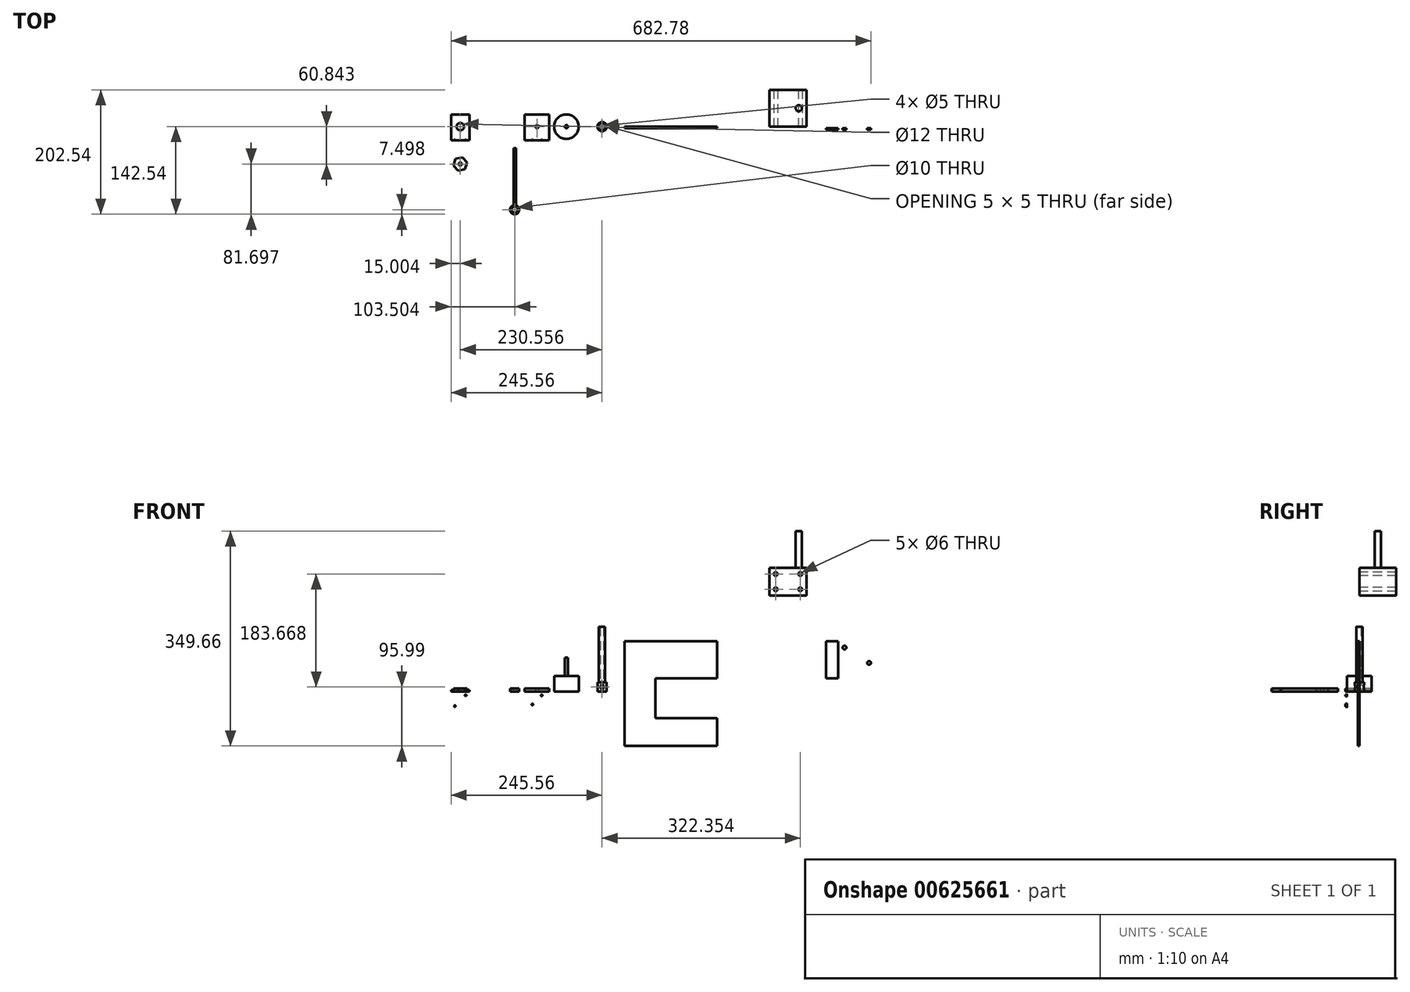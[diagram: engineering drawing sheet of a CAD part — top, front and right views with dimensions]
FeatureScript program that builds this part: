
annotation { "Feature Type Name" : "Feature", "Feature Type Description" : "" }
export const myFeature = defineFeature(function(context is Context, id is Id, definition is map)
    precondition{}
    {
        {
            var Q0;
            Q0=qCreatedBy(makeId("Top.planeOp"),FACE);
            var sketch = newSketch(context, id + "F0", { "sketchPlane" : qUnion([Q0])});
            skCircle(sketch, "E0", {"center": v(0, 0) * mm, "radius": 2.5 * mm});
            skCircle(sketch, "E1", {"center": v(0, 0) * mm, "radius": 7.5 * mm});
            skLineSegment(sketch, "E2", {"start": v(-20, 7.5) * mm, "end": v(20, 7.5) * mm});
            skCircle(sketch, "E3", {"center": v(-57.97, 0) * mm, "radius": 20 * mm});
            skLineSegment(sketch, "E4.bottom", {"start": v(-125.74, 20) * mm, "end": v(-85.74, 20) * mm});
            skLineSegment(sketch, "E4.top", {"start": v(-125.74, -20) * mm, "end": v(-85.74, -20) * mm});
            skLineSegment(sketch, "E4.left", {"start": v(-125.74, 20) * mm, "end": v(-125.74, -20) * mm});
            skLineSegment(sketch, "E4.right", {"start": v(-85.74, 20) * mm, "end": v(-85.74, -20) * mm});
            skPoint(sketch, "E4.middle", {"position": v(-105.74, 0) * mm});
            skCircle(sketch, "E5", {"center": v(-105.74, 0) * mm, "radius": 2.5 * mm});
            skLineSegment(sketch, "E6.bottom", {"start": v(-215.56, 20) * mm, "end": v(-245.56, 20) * mm});
            skLineSegment(sketch, "E6.top", {"start": v(-215.56, -20) * mm, "end": v(-245.56, -20) * mm});
            skLineSegment(sketch, "E6.left", {"start": v(-215.56, 20) * mm, "end": v(-215.56, -20) * mm});
            skLineSegment(sketch, "E6.right", {"start": v(-245.56, 20) * mm, "end": v(-245.56, -20) * mm});
            skCircle(sketch, "E7", {"center": v(-230.56, 0) * mm, "radius": 6 * mm});
            skPoint(sketch, "E7.centerSnap0", {"position": v(-230.56, 20) * mm});
            skCircle(sketch, "E8.cCircle", {"center": v(-230.56, -60.84) * mm, "radius": 9.88 * mm, "construction": true});
            skLineSegment(sketch, "E8.0", {"start": v(-219.4, -58.45) * mm, "end": v(-222.9, -69.3) * mm});
            skLineSegment(sketch, "E8.1", {"start": v(-222.9, -69.3) * mm, "end": v(-234.06, -71.7) * mm});
            skLineSegment(sketch, "E8.2", {"start": v(-234.06, -71.7) * mm, "end": v(-241.71, -63.24) * mm});
            skLineSegment(sketch, "E8.3", {"start": v(-241.71, -63.24) * mm, "end": v(-238.21, -52.38) * mm});
            skLineSegment(sketch, "E8.4", {"start": v(-238.21, -52.38) * mm, "end": v(-227.05, -49.98) * mm});
            skLineSegment(sketch, "E8.5", {"start": v(-227.05, -49.98) * mm, "end": v(-219.4, -58.45) * mm});
            skPoint(sketch, "E8.0.midPoint", {"position": v(-221.15, -63.88) * mm});
            skCircle(sketch, "E9", {"center": v(-230.56, -60.84) * mm, "radius": 2.5 * mm});
            skCircle(sketch, "E10", {"center": v(-142.06, -135.04) * mm, "radius": 5 * mm});
            skArc(sketch, "E11", {"start": v(-144.06, -127.81) * mm, "mid": v(-142.06, -142.54) * mm, "end": v(-140.06, -127.81) * mm});
            skLineSegment(sketch, "E12", {"start": v(-140.06, -127.81) * mm, "end": v(-140.06, -35.04) * mm});
            skLineSegment(sketch, "E13", {"start": v(-140.06, -35.04) * mm, "end": v(-142.06, -35.04) * mm});
            skLineSegment(sketch, "E14.MirrorCS", {"start": v(-144.06, -127.81) * mm, "end": v(-144.06, -35.04) * mm});
            skLineSegment(sketch, "E15", {"start": v(-142.06, -35.04) * mm, "end": v(-144.06, -35.04) * mm});
            skSolve(sketch);
        }
        {
            var Q0;
            Q0=makeQuery(id+"F0.imprint","IMPRINT",FACE,{"disambiguationData":[TD([[makeQuery(id+"F0.imprint","IMPRINT",EDGE,{"derivedFrom":sQuery(id+"F0.wireOp",EDGE,"E0")}),-1.0]])]});
            extrude(context, id + "F1", {"entities" : qUnion([Q0]), "depth" : 15 * mm, "offsetDistance" : 25 * mm});
        }
        {
            var Q0;
            Q0=makeQuery(id+"F1.opExtrude","CAP_FACE",FACE,{"disambiguationData":[OSD([sQuery(id+"F0.wireOp",EDGE,"E0"),sQuery(id+"F0.wireOp",EDGE,"E1")])],"isStart":false});
            var sketch = newSketch(context, id + "F2", { "sketchPlane" : qUnion([Q0])});
            skCircle(sketch, "E16", {"center": v(0, 0) * mm, "radius": 5 * mm});
            skSolve(sketch);
        }
        {
            var Q0;
            Q0=makeQuery(id+"F2.imprint","IMPRINT",FACE,{"disambiguationData":[TD([[makeQuery(id+"F2.imprint","IMPRINT",EDGE,{"derivedFrom":sQuery(id+"F2.wireOp",EDGE,"E16")}),1.0]])]});
            extrude(context, id + "F3", {"entities" : qUnion([Q0]), "operationType" : NewBodyOperationType.ADD, "depth" : 90 * mm, "offsetDistance" : 25 * mm});
        }
        {
            var Q0;
            Q0=sQuery(id+"F0.wireOp",EDGE,"E2");
            extrude(context, id + "F4", {"bodyType" : ToolBodyType.SURFACE, "surfaceEntities" : qUnion([Q0]), "depth" : 15 * mm, "offsetDistance" : 25 * mm});
        }
        {
            var Q0;
            Q0=makeQuery(id+"F4.opExtrude","SWEPT_FACE",FACE,{"disambiguationData":[OSD([sQuery(id+"F0.wireOp",EDGE,"E2")])]});
            var sketch = newSketch(context, id + "F5", { "sketchPlane" : qUnion([Q0])});
            skCircle(sketch, "E17", {"center": v(0, 7.5) * mm, "radius": 3 * mm});
            skPoint(sketch, "E17.centerSnap0", {"position": v(-20, 7.5) * mm});
            skSolve(sketch);
        }
        {
            var Q0;
            Q0=makeQuery(id+"F5.imprint","IMPRINT",FACE,{"disambiguationData":[TD([[makeQuery(id+"F5.imprint","IMPRINT",EDGE,{"derivedFrom":sQuery(id+"F5.wireOp",EDGE,"E17")}),1.0]])]});
            extrude(context, id + "F6", {"entities" : qUnion([Q0]), "operationType" : NewBodyOperationType.REMOVE, "endBound" : BoundingType.THROUGH_ALL, "depth" : 25 * mm, "offsetDistance" : 25 * mm});
        }
        {
            var Q0;
            Q0=makeQuery(id+"F0.imprint","IMPRINT",FACE,{"disambiguationData":[TD([[makeQuery(id+"F0.imprint","IMPRINT",EDGE,{"derivedFrom":sQuery(id+"F0.wireOp",EDGE,"E3")}),1.0]])]});
            extrude(context, id + "F7", {"entities" : qUnion([Q0]), "depth" : 25 * mm, "offsetDistance" : 25 * mm});
        }
        {
            var Q0;
            Q0=makeQuery(id+"F7.opExtrude","CAP_FACE",FACE,{"disambiguationData":[OSD([sQuery(id+"F0.wireOp",EDGE,"E3")])],"isStart":false});
            var sketch = newSketch(context, id + "F8", { "sketchPlane" : qUnion([Q0])});
            skCircle(sketch, "E18", {"center": v(-57.97, 0) * mm, "radius": 2.5 * mm});
            skSolve(sketch);
        }
        {
            var Q0;
            Q0=makeQuery(id+"F8.imprint","IMPRINT",FACE,{"disambiguationData":[TD([[makeQuery(id+"F8.imprint","IMPRINT",EDGE,{"derivedFrom":sQuery(id+"F8.wireOp",EDGE,"E18")}),1.0]])]});
            extrude(context, id + "F9", {"entities" : qUnion([Q0]), "operationType" : NewBodyOperationType.ADD, "depth" : 30 * mm, "offsetDistance" : 25 * mm});
        }
        {
            var Q0;
            Q0=makeQuery(id+"F0.imprint","IMPRINT",FACE,{"disambiguationData":[TD([[makeQuery(id+"F0.imprint","IMPRINT",EDGE,{"derivedFrom":sQuery(id+"F0.wireOp",EDGE,"E4.bottom")}),-1.0]])]});
            extrude(context, id + "F10", {"entities" : qUnion([Q0]), "depth" : 5 * mm, "offsetDistance" : 25 * mm});
        }
        {
            var Q0;
            Q0=makeQuery(id+"F10.opExtrude","CAP_FACE",FACE,{"disambiguationData":[OSD([sQuery(id+"F0.wireOp",EDGE,"E4.bottom"),sQuery(id+"F0.wireOp",EDGE,"E4.top"),sQuery(id+"F0.wireOp",EDGE,"E4.left"),sQuery(id+"F0.wireOp",EDGE,"E4.right"),sQuery(id+"F0.wireOp",EDGE,"E5")])],"isStart":false});
            var sketch = newSketch(context, id + "F11", { "sketchPlane" : qUnion([Q0])});
            skLineSegment(sketch, "E19.bottom", {"start": v(-125.74, -20) * mm, "end": v(-85.74, -20) * mm});
            skLineSegment(sketch, "E19.top", {"start": v(-125.74, -22.5) * mm, "end": v(-85.74, -22.5) * mm});
            skLineSegment(sketch, "E19.left", {"start": v(-125.74, -20) * mm, "end": v(-125.74, -22.5) * mm});
            skLineSegment(sketch, "E19.right", {"start": v(-85.74, -20) * mm, "end": v(-85.74, -22.5) * mm});
            skSolve(sketch);
        }
        {
            var Q0;
            Q0=makeQuery(id+"F11.imprint","IMPRINT",FACE,{"disambiguationData":[TD([[makeQuery(id+"F11.imprint","IMPRINT",EDGE,{"derivedFrom":sQuery(id+"F11.wireOp",EDGE,"E19.bottom")}),-1.0]])]});
            extrude(context, id + "F12", {"entities" : qUnion([Q0]), "operationType" : NewBodyOperationType.ADD, "oppositeDirection" : true, "depth" : 32.5 * mm, "offsetDistance" : 25 * mm});
        }
        {
            var Q0;
            Q0=qCreatedBy(makeId("Front.planeOp"),FACE);
            var sketch = newSketch(context, id + "F13", { "sketchPlane" : qUnion([Q0])});
            skLineSegment(sketch, "E20.bottom", {"start": v(36.88, 81.5) * mm, "end": v(186.88, 81.5) * mm});
            skLineSegment(sketch, "E20.top", {"start": v(36.88, -88.5) * mm, "end": v(186.88, -88.5) * mm});
            skLineSegment(sketch, "E20.left", {"start": v(36.88, 81.5) * mm, "end": v(36.88, -88.5) * mm});
            skLineSegment(sketch, "E20.right", {"start": v(186.88, 81.5) * mm, "end": v(186.88, -88.5) * mm});
            skLineSegment(sketch, "E21", {"start": v(186.88, 21.5) * mm, "end": v(86.88, 21.5) * mm});
            skLineSegment(sketch, "E22", {"start": v(186.88, -43.5) * mm, "end": v(86.88, -43.5) * mm});
            skLineSegment(sketch, "E23", {"start": v(86.88, 21.5) * mm, "end": v(86.88, -43.5) * mm});
            skLineSegment(sketch, "E24.bottom", {"start": v(272.35, 201.17) * mm, "end": v(332.35, 201.17) * mm});
            skLineSegment(sketch, "E24.top", {"start": v(272.35, 156.17) * mm, "end": v(332.35, 156.17) * mm});
            skLineSegment(sketch, "E24.left", {"start": v(272.35, 201.17) * mm, "end": v(272.35, 156.17) * mm});
            skLineSegment(sketch, "E24.right", {"start": v(332.35, 201.17) * mm, "end": v(332.35, 156.17) * mm});
            skCircle(sketch, "E25", {"center": v(322.35, 191.17) * mm, "radius": 3 * mm});
            skLineSegment(sketch, "E26", {"start": v(272.35, 178.67) * mm, "end": v(332.35, 178.67) * mm, "construction": true});
            skLineSegment(sketch, "E27", {"start": v(302.35, 156.17) * mm, "end": v(302.35, 201.17) * mm, "construction": true});
            skCircle(sketch, "E28.MirrorC", {"center": v(282.35, 191.17) * mm, "radius": 3 * mm});
            skCircle(sketch, "E29.MirrorC", {"center": v(282.35, 166.17) * mm, "radius": 3 * mm});
            skCircle(sketch, "E30.MirrorC", {"center": v(322.35, 166.17) * mm, "radius": 3 * mm});
            skSolve(sketch);
        }
        {
            var Q0;
            {var subQ1=sQuery(id+"F13.wireOp",EDGE,"E20.bottom");Q0=makeQuery(id+"F13.imprint","IMPRINT",FACE,{"disambiguationData":[TD([[makeQuery(id+"F13.imprint","IMPRINT",EDGE,{"derivedFrom":subQ1}),-1.0]])]});}
            extrude(context, id + "F14", {"entities" : qUnion([Q0]), "depth" : 2.5 * mm, "offsetDistance" : 25 * mm});
        }
        {
            var Q0;
            Q0=makeQuery(id+"F14.opExtrude","CAP_FACE",FACE,{"disambiguationData":[OSD([sQuery(id+"F13.wireOp",EDGE,"E20.bottom"),sQuery(id+"F13.wireOp",EDGE,"E20.top"),sQuery(id+"F13.wireOp",EDGE,"E20.left"),sQuery(id+"F13.wireOp",EDGE,"E20.right"),sQuery(id+"F13.wireOp",EDGE,"E21"),sQuery(id+"F13.wireOp",EDGE,"E22"),sQuery(id+"F13.wireOp",EDGE,"E23")])],"isStart":false});
            var sketch = newSketch(context, id + "F15", { "sketchPlane" : qUnion([Q0])});
            skLineSegment(sketch, "E31", {"start": v(186.88, 49) * mm, "end": v(86.88, 49) * mm});
            skLineSegment(sketch, "E32", {"start": v(86.88, 49) * mm, "end": v(86.88, 21.5) * mm});
            skLineSegment(sketch, "E33", {"start": v(186.88, -43.5) * mm, "end": v(86.88, -43.5) * mm});
            skLineSegment(sketch, "E34", {"start": v(86.88, -43.5) * mm, "end": v(86.88, -43.5) * mm});
            skLineSegment(sketch, "E35", {"start": v(86.88, 49) * mm, "end": v(86.88, 81.5) * mm});
            skLineSegment(sketch, "E36", {"start": v(86.88, 81.5) * mm, "end": v(86.88, -88.5) * mm});
            skLineSegment(sketch, "E37.bottom", {"start": v(364.22, 81.5) * mm, "end": v(444.22, 81.5) * mm});
            skLineSegment(sketch, "E37.top", {"start": v(384.22, 36.5) * mm, "end": v(444.22, 36.5) * mm});
            skLineSegment(sketch, "E37.right", {"start": v(444.22, 81.5) * mm, "end": v(444.22, 36.5) * mm});
            skLineSegment(sketch, "E38", {"start": v(384.22, 36.5) * mm, "end": v(384.22, 21.5) * mm});
            skLineSegment(sketch, "E39", {"start": v(384.22, 21.5) * mm, "end": v(364.22, 21.5) * mm});
            skLineSegment(sketch, "E40", {"start": v(364.22, 81.5) * mm, "end": v(364.22, 21.5) * mm});
            skSolve(sketch);
        }
        {
            var Q0;
            Q0=makeQuery(id+"F0.imprint","IMPRINT",FACE,{"disambiguationData":[TD([[makeQuery(id+"F0.imprint","IMPRINT",EDGE,{"derivedFrom":sQuery(id+"F0.wireOp",EDGE,"E6.bottom")}),1.0]])]});
            extrude(context, id + "F16", {"entities" : qUnion([Q0]), "depth" : 2.5 * mm, "offsetDistance" : 25 * mm});
        }
        {
            var Q0;
            Q0=makeQuery(id+"F16.opExtrude","CAP_FACE",FACE,{"disambiguationData":[OSD([sQuery(id+"F0.wireOp",EDGE,"E6.bottom"),sQuery(id+"F0.wireOp",EDGE,"E6.top"),sQuery(id+"F0.wireOp",EDGE,"E6.left"),sQuery(id+"F0.wireOp",EDGE,"E6.right"),sQuery(id+"F0.wireOp",EDGE,"E7")])],"isStart":false});
            var sketch = newSketch(context, id + "F17", { "sketchPlane" : qUnion([Q0])});
            skLineSegment(sketch, "E41.bottom", {"start": v(-245.56, -20) * mm, "end": v(-215.56, -20) * mm});
            skLineSegment(sketch, "E41.top", {"start": v(-245.56, -22.5) * mm, "end": v(-215.56, -22.5) * mm});
            skLineSegment(sketch, "E41.left", {"start": v(-245.56, -20) * mm, "end": v(-245.56, -22.5) * mm});
            skLineSegment(sketch, "E41.right", {"start": v(-215.56, -20) * mm, "end": v(-215.56, -22.5) * mm});
            skSolve(sketch);
        }
        {
            var Q0;
            Q0=makeQuery(id+"F17.imprint","IMPRINT",FACE,{"disambiguationData":[TD([[makeQuery(id+"F17.imprint","IMPRINT",EDGE,{"derivedFrom":sQuery(id+"F17.wireOp",EDGE,"E41.bottom")}),1.0]])]});
            extrude(context, id + "F18", {"entities" : qUnion([Q0]), "operationType" : NewBodyOperationType.ADD, "oppositeDirection" : true, "depth" : 32.5 * mm, "offsetDistance" : 25 * mm});
        }
        {
            var Q0;
            Q0=makeQuery(id+"F0.imprint","IMPRINT",FACE,{"disambiguationData":[TD([[makeQuery(id+"F0.imprint","IMPRINT",EDGE,{"derivedFrom":sQuery(id+"F0.wireOp",EDGE,"E8.0")}),-1.0]])]});
            extrude(context, id + "F19", {"entities" : qUnion([Q0]), "depth" : 5 * mm, "offsetDistance" : 25 * mm});
        }
        {
            var Q0;
            Q0=makeQuery(id+"F12.opExtrude","SWEPT_FACE",FACE,{"disambiguationData":[OSD([sQuery(id+"F11.wireOp",EDGE,"E19.bottom")])]});
            var sketch = newSketch(context, id + "F20", { "sketchPlane" : qUnion([Q0])});
            skCircle(sketch, "E42", {"center": v(113.24, -6.25) * mm, "radius": 1.25 * mm});
            skLineSegment(sketch, "E43", {"start": v(105.74, 0) * mm, "end": v(105.74, -27.5) * mm, "construction": true});
            skLineSegment(sketch, "E44", {"start": v(125.74, -13.75) * mm, "end": v(85.74, -13.75) * mm, "construction": true});
            skCircle(sketch, "E45.MirrorC", {"center": v(98.24, -6.25) * mm, "radius": 1.25 * mm});
            skCircle(sketch, "E46.MirrorC", {"center": v(98.24, -21.25) * mm, "radius": 1.25 * mm});
            skCircle(sketch, "E47.MirrorC", {"center": v(113.24, -21.25) * mm, "radius": 1.25 * mm});
            skSolve(sketch);
        }
        {
            var Q0;
            Q0=makeQuery(id+"F20.imprint","IMPRINT",FACE,{"disambiguationData":[TD([[makeQuery(id+"F20.imprint","IMPRINT",EDGE,{"derivedFrom":sQuery(id+"F20.wireOp",EDGE,"E45.MirrorC")}),-1.0]])]});
            var Q1;
            Q1=makeQuery(id+"F20.imprint","IMPRINT",FACE,{"disambiguationData":[TD([[makeQuery(id+"F20.imprint","IMPRINT",EDGE,{"derivedFrom":sQuery(id+"F20.wireOp",EDGE,"E42")}),1.0]])]});
            var Q2;
            Q2=makeQuery(id+"F20.imprint","IMPRINT",FACE,{"disambiguationData":[TD([[makeQuery(id+"F20.imprint","IMPRINT",EDGE,{"derivedFrom":sQuery(id+"F20.wireOp",EDGE,"E47.MirrorC")}),-1.0]])]});
            var Q3;
            Q3=makeQuery(id+"F20.imprint","IMPRINT",FACE,{"disambiguationData":[TD([[makeQuery(id+"F20.imprint","IMPRINT",EDGE,{"derivedFrom":sQuery(id+"F20.wireOp",EDGE,"E46.MirrorC")}),1.0]])]});
            extrude(context, id + "F21", {"entities" : qUnion([Q0, Q1, Q2, Q3]), "operationType" : NewBodyOperationType.REMOVE, "endBound" : BoundingType.UP_TO_NEXT, "oppositeDirection" : true, "depth" : 25 * mm, "offsetDistance" : 25 * mm});
        }
        {
            var Q0;
            Q0=makeQuery(id+"F18.opExtrude","SWEPT_FACE",FACE,{"disambiguationData":[OSD([sQuery(id+"F17.wireOp",EDGE,"E41.bottom")])]});
            var sketch = newSketch(context, id + "F22", { "sketchPlane" : qUnion([Q0])});
            skLineSegment(sketch, "E48", {"start": v(230.56, 0) * mm, "end": v(230.56, -30) * mm, "construction": true});
            skLineSegment(sketch, "E49", {"start": v(215.56, -15) * mm, "end": v(245.56, -15) * mm, "construction": true});
            skCircle(sketch, "E50", {"center": v(239.3, -6.25) * mm, "radius": 1.25 * mm});
            skCircle(sketch, "E51.MirrorC", {"center": v(221.8, -6.25) * mm, "radius": 1.25 * mm});
            skCircle(sketch, "E52.MirrorC", {"center": v(221.8, -23.75) * mm, "radius": 1.25 * mm});
            skCircle(sketch, "E53.MirrorC", {"center": v(239.3, -23.75) * mm, "radius": 1.25 * mm});
            skSolve(sketch);
        }
        {
            var Q0;
            Q0=makeQuery(id+"F22.imprint","IMPRINT",FACE,{"disambiguationData":[TD([[makeQuery(id+"F22.imprint","IMPRINT",EDGE,{"derivedFrom":sQuery(id+"F22.wireOp",EDGE,"E51.MirrorC")}),-1.0]])]});
            var Q1;
            Q1=makeQuery(id+"F22.imprint","IMPRINT",FACE,{"disambiguationData":[TD([[makeQuery(id+"F22.imprint","IMPRINT",EDGE,{"derivedFrom":sQuery(id+"F22.wireOp",EDGE,"E52.MirrorC")}),1.0]])]});
            var Q2;
            Q2=makeQuery(id+"F22.imprint","IMPRINT",FACE,{"disambiguationData":[TD([[makeQuery(id+"F22.imprint","IMPRINT",EDGE,{"derivedFrom":sQuery(id+"F22.wireOp",EDGE,"E53.MirrorC")}),-1.0]])]});
            var Q3;
            Q3=makeQuery(id+"F22.imprint","IMPRINT",FACE,{"disambiguationData":[TD([[makeQuery(id+"F22.imprint","IMPRINT",EDGE,{"derivedFrom":sQuery(id+"F22.wireOp",EDGE,"E50")}),1.0]])]});
            extrude(context, id + "F23", {"entities" : qUnion([Q0, Q1, Q2, Q3]), "operationType" : NewBodyOperationType.REMOVE, "endBound" : BoundingType.UP_TO_NEXT, "oppositeDirection" : true, "depth" : 25 * mm, "offsetDistance" : 25 * mm});
        }
        {
            var Q0;
            Q0=makeQuery(id+"F13.imprint","IMPRINT",FACE,{"disambiguationData":[TD([[makeQuery(id+"F13.imprint","IMPRINT",EDGE,{"derivedFrom":sQuery(id+"F13.wireOp",EDGE,"E24.bottom")}),-1.0]])]});
            extrude(context, id + "F24", {"entities" : qUnion([Q0]), "oppositeDirection" : true, "depth" : 60 * mm, "offsetDistance" : 25 * mm});
        }
        {
            var Q0;
            Q0=makeQuery(id+"F24.opExtrude","SWEPT_FACE",FACE,{"disambiguationData":[OSD([sQuery(id+"F13.wireOp",EDGE,"E24.bottom")])]});
            var sketch = newSketch(context, id + "F25", { "sketchPlane" : qUnion([Q0])});
            skCircle(sketch, "E54", {"center": v(319.85, 30) * mm, "radius": 5 * mm});
            skCircle(sketch, "E55", {"center": v(319.85, 30) * mm, "radius": 12.5 * mm, "construction": true});
            skSolve(sketch);
        }
        {
            var Q0;
            Q0=makeQuery(id+"F25.imprint","IMPRINT",FACE,{"disambiguationData":[TD([[makeQuery(id+"F25.imprint","IMPRINT",EDGE,{"derivedFrom":sQuery(id+"F25.wireOp",EDGE,"E54")}),1.0]])]});
            extrude(context, id + "F26", {"entities" : qUnion([Q0]), "operationType" : NewBodyOperationType.ADD, "depth" : 60 * mm, "offsetDistance" : 25 * mm});
        }
        {
            var Q0;
            Q0=makeQuery(id+"F15.imprint","IMPRINT",FACE,{"disambiguationData":[TD([[makeQuery(id+"F15.imprint","IMPRINT",EDGE,{"derivedFrom":sQuery(id+"F15.wireOp",EDGE,"E37.bottom")}),-1.0]])]});
            extrude(context, id + "F27", {"entities" : qUnion([Q0]), "depth" : 2.5 * mm, "offsetDistance" : 25 * mm});
        }
        {
            var Q0;
            Q0=makeQuery(id+"F27.opExtrude","CAP_FACE",FACE,{"disambiguationData":[OSD([sQuery(id+"F15.wireOp",EDGE,"E37.bottom"),sQuery(id+"F15.wireOp",EDGE,"E37.top"),sQuery(id+"F15.wireOp",EDGE,"E37.left"),sQuery(id+"F15.wireOp",EDGE,"E37.right")])],"isStart":false});
            var sketch = newSketch(context, id + "F28", { "sketchPlane" : qUnion([Q0])});
            skLineSegment(sketch, "E56", {"start": v(384.22, 81.5) * mm, "end": v(384.22, 36.5) * mm});
            skLineSegment(sketch, "E57", {"start": v(414.22, 36.5) * mm, "end": v(414.22, 81.5) * mm, "construction": true});
            skLineSegment(sketch, "E58", {"start": v(444.22, 59) * mm, "end": v(384.22, 59) * mm, "construction": true});
            skCircle(sketch, "E59", {"center": v(434.22, 71.5) * mm, "radius": 3 * mm});
            skCircle(sketch, "E60.MirrorC", {"center": v(394.22, 71.5) * mm, "radius": 3 * mm});
            skCircle(sketch, "E61.MirrorC", {"center": v(394.22, 46.5) * mm, "radius": 3 * mm});
            skCircle(sketch, "E62.MirrorC", {"center": v(434.22, 46.5) * mm, "radius": 3 * mm});
            skSolve(sketch);
        }
        {
            var Q0;
            Q0=makeQuery(id+"F28.imprint","IMPRINT",FACE,{"disambiguationData":[TD([[makeQuery(id+"F28.imprint","IMPRINT",EDGE,{"derivedFrom":sQuery(id+"F28.wireOp",EDGE,"E60.MirrorC")}),-1.0]])]});
            var Q1;
            Q1=makeQuery(id+"F28.imprint","IMPRINT",FACE,{"disambiguationData":[TD([[makeQuery(id+"F28.imprint","IMPRINT",EDGE,{"derivedFrom":sQuery(id+"F28.wireOp",EDGE,"E61.MirrorC")}),1.0]])]});
            var Q2;
            Q2=makeQuery(id+"F28.imprint","IMPRINT",FACE,{"disambiguationData":[TD([[makeQuery(id+"F28.imprint","IMPRINT",EDGE,{"derivedFrom":sQuery(id+"F28.wireOp",EDGE,"E59")}),1.0]])]});
            var Q3;
            Q3=makeQuery(id+"F28.imprint","IMPRINT",FACE,{"disambiguationData":[TD([[makeQuery(id+"F28.imprint","IMPRINT",EDGE,{"derivedFrom":sQuery(id+"F28.wireOp",EDGE,"E62.MirrorC")}),-1.0]])]});
            extrude(context, id + "F29", {"entities" : qUnion([Q0, Q1, Q2, Q3]), "operationType" : NewBodyOperationType.REMOVE, "oppositeDirection" : true, "depth" : 25 * mm, "offsetDistance" : 25 * mm});
        }
        {
            var Q0;
            Q0=makeQuery(id+"F0.imprint","IMPRINT",FACE,{"disambiguationData":[TD([[makeQuery(id+"F0.imprint","IMPRINT",EDGE,{"derivedFrom":sQuery(id+"F0.wireOp",EDGE,"E10")}),-1.0]])]});
            extrude(context, id + "F30", {"entities" : qUnion([Q0]), "depth" : 5 * mm, "offsetDistance" : 25 * mm});
        }
    });
